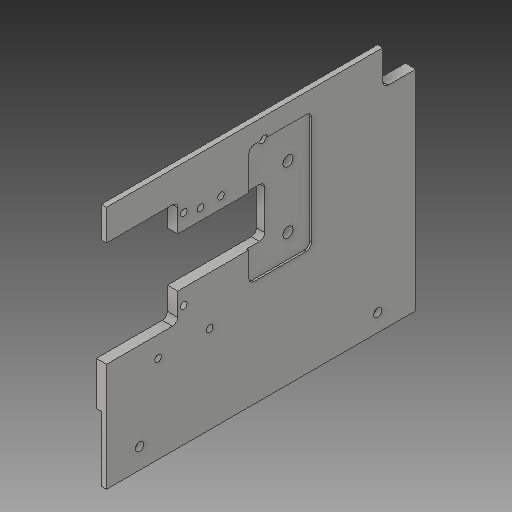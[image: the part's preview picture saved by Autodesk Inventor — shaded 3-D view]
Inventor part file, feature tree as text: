
AUTODESK INVENTOR PART (.ipt)
format: ipt  version: 2018 (Build 220112000, 112)  size: 229,376 bytes
history: native  units: mm
features: reference x9, extrude x8, sketch x8, other x7, fillet x2
ambient origin geometry x8: Origin, YZ Plane, XZ Plane, XY Plane, X Axis, Y Axis, Z Axis, Center Point
bodies: Solid1 (feature_tree)
feature tree (34):
  extrude  "Extrusion1"  Depth=237.0mm
  extrude  "Extrusion2"  Depth=32.0mm
  extrude  "Extrusion3"  Depth=5.0mm
  extrude  "Extrusion4"  Depth=138.0mm
  extrude  "Extrusion5"  Depth=61.0mm
  extrude  "Extrusion6"  Depth=5.0mm
  fillet  "Fillet1"  Radius=2.0mm
  extrude  "Extrusion7"  Depth=32.0mm
  fillet  "Fillet2"  Radius=20.0mm
  extrude  "Extrusion8"  Depth=10.0mm
  sketch  "Sketch1"  dims[d0=300.0mm d1=237.0mm]
  sketch  "Sketch2"  dims[d2=10.0mm d3=0.0mm d4=32.0mm]
  sketch  "Sketch3"  dims[d5=34.0mm d6=5.0mm]
  sketch  "Sketch4"  dims[d7=10.0mm d8=0.0mm d9=138.0mm]
  sketch  "Sketch5"  dims[d10=115.0mm d11=61.0mm]
  sketch  "Sketch6"  dims[d12=19.0mm d13=5.0mm d14=2.0mm d15=0.0mm]
  sketch  "Sketch7"  dims[d16=8.0mm d17=32.0mm d18=20.0mm]
  reference  "Reference1"
  reference  "Reference2"
  reference  "Reference3"
  sketch  "Sketch8"  dims[d19=17.0mm d20=37.0mm d21=153.0mm d22=20.0mm d23=2.0mm d24=0.0mm d25=70.0mm d26=63.0mm d27=63.0mm d28=67.0mm d29=5.0mm d30=0.0mm d31=122.0mm d32=10.0mm d34=60.0mm d35=51.0mm d36=5.0mm d37=0.0mm d38=5.0mm d39=30.0mm d40=102.0mm d41=57.0mm d42=10.0mm d43=48.0mm d44=10.0mm d45=0.0mm d46=5.0mm d47=10.0mm d48=0.0mm d49=0.25mm d50=0.25mm d51=0.25mm d52=0.25mm d53=0.25mm d54=0.25mm]
  reference  "Reference4"
  reference  "Reference5"
  reference  "Reference6"
  reference  "Reference7"
  reference  "Reference8"
  reference  "Reference9"
  parser-record x1  (decoder bookkeeping rows leaked as tree rows — omitted from the tree; the rows remain in map.json)
  other  "Lathe Model V3.iam"
  other  "MotorHolderLongAxis:1"
  other  "BNT 2010-2_6 +1166L C7T-J1K_10000KBK 15BF 15:1"
  other  "BK 15:1"
  other  "MotorHolderLongAxisBottom:1"
  other  "MotorHolderLongAxisTop:1"
note: 1 file-system path scrubbed to <path> (originals preserved in map.json)
